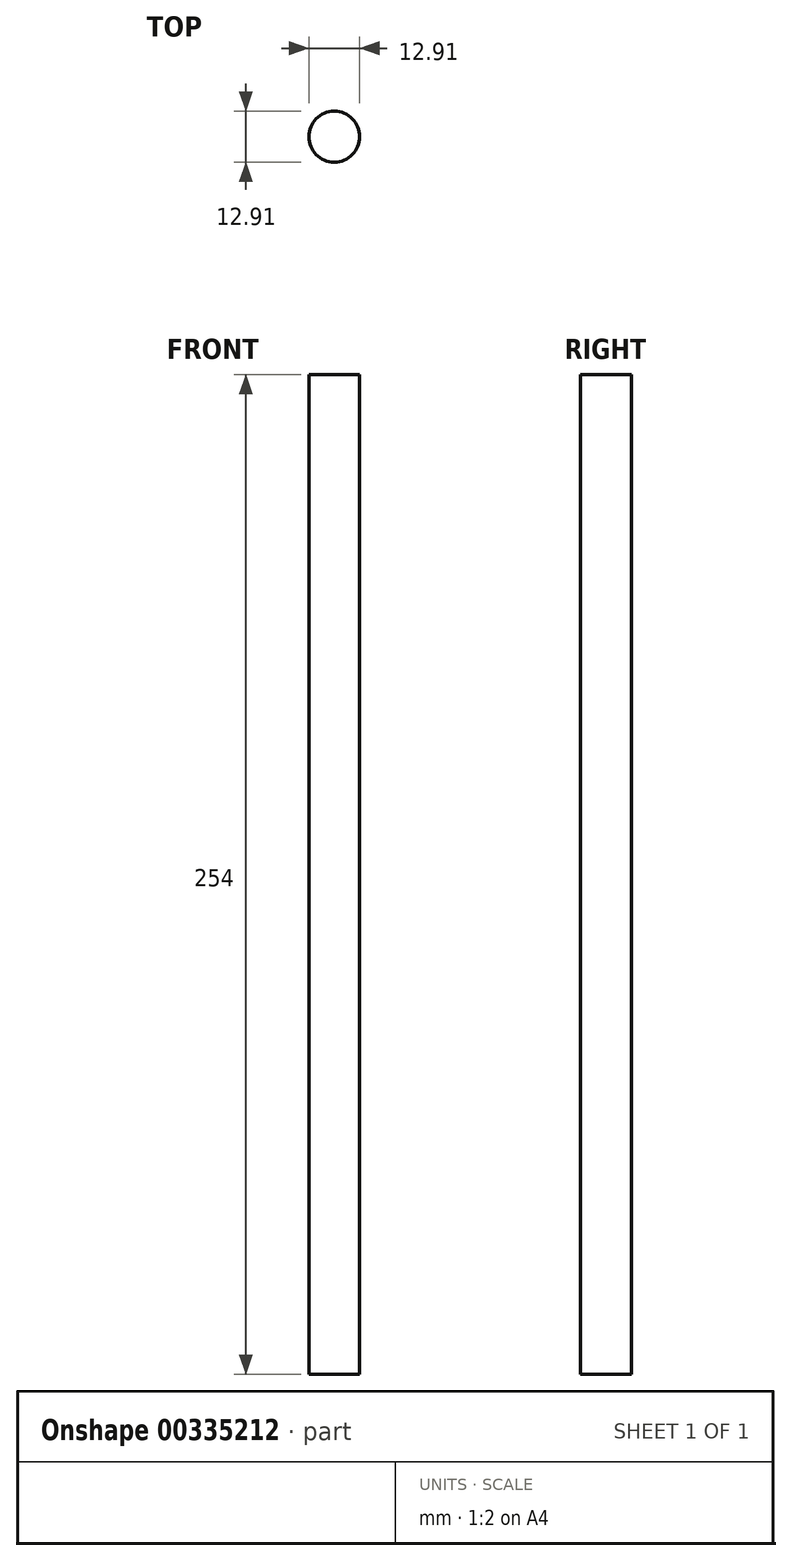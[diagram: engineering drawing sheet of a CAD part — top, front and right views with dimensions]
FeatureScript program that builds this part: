
annotation { "Feature Type Name" : "Feature", "Feature Type Description" : "" }
export const myFeature = defineFeature(function(context is Context, id is Id, definition is map)
    precondition{}
    {
        {
            var Q0;
            Q0=qCreatedBy(makeId("Top.planeOp"),FACE);
            var sketch = newSketch(context, id + "F0", { "sketchPlane" : qUnion([Q0])});
            skCircle(sketch, "E0", {"center": v(-35.89, 15.88) * mm, "radius": 6.46 * mm});
            skCircle(sketch, "E1", {"center": v(-35.89, 15.88) * mm, "radius": 4.74 * mm});
            skSolve(sketch);
        }
        {
            var Q0;
            Q0=makeQuery(id+"F0.imprint","IMPRINT",FACE,{"disambiguationData":[TD([[makeQuery(id+"F0.imprint","IMPRINT",EDGE,{"derivedFrom":sQuery(id+"F0.wireOp",EDGE,"E0")}),1.0]])]});
            var Q1;
            Q1=makeQuery(id+"F0.imprint","IMPRINT",FACE,{"disambiguationData":[TD([[makeQuery(id+"F0.imprint","IMPRINT",EDGE,{"derivedFrom":sQuery(id+"F0.wireOp",EDGE,"E1")}),1.0]])]});
            extrude(context, id + "F1", {"entities" : qUnion([Q0, Q1]), "depth" : 254 * mm});
        }
    });
